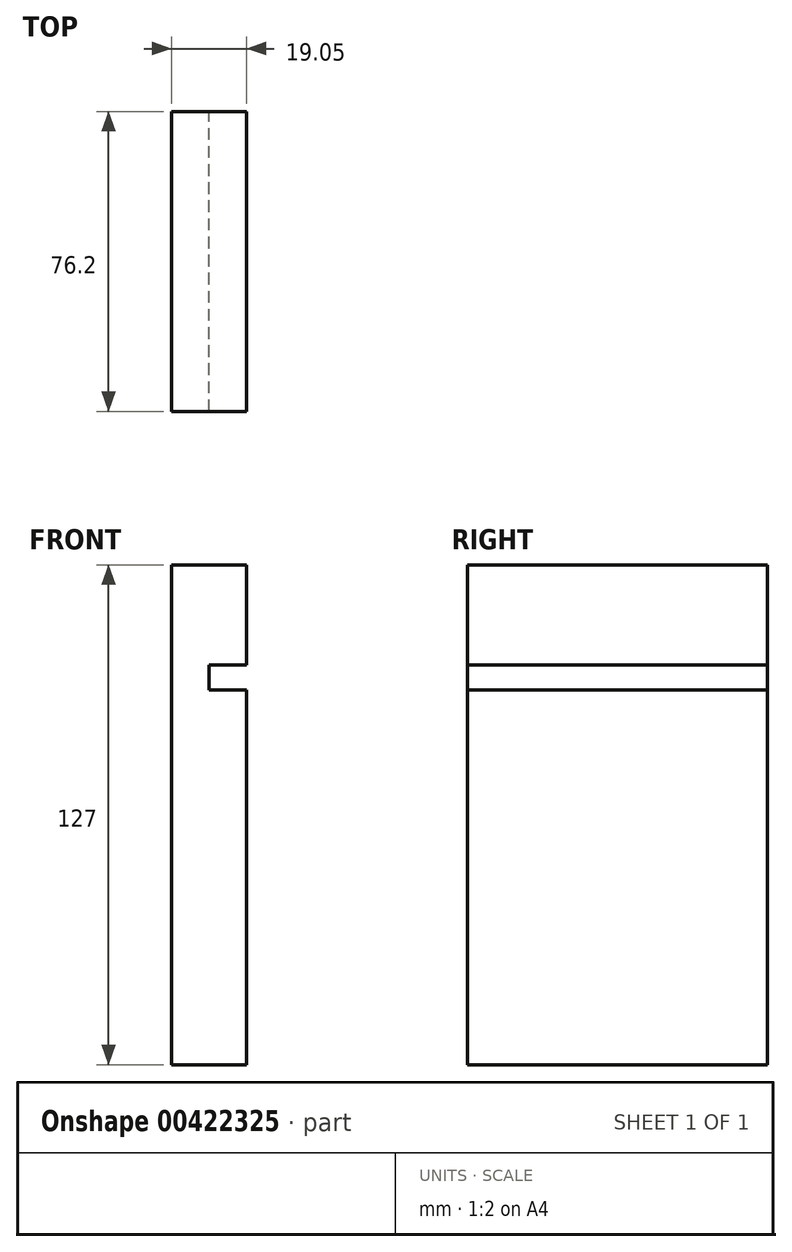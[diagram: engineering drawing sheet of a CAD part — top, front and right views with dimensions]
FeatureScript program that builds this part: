
annotation { "Feature Type Name" : "Feature", "Feature Type Description" : "" }
export const myFeature = defineFeature(function(context is Context, id is Id, definition is map)
    precondition{}
    {
        {
            var Q0;
            Q0=qCreatedBy(makeId("Front.planeOp"),FACE);
            var sketch = newSketch(context, id + "F0", { "sketchPlane" : qUnion([Q0])});
            skLineSegment(sketch, "E0", {"start": v(-41.47, 68.64) * mm, "end": v(-41.47, -58.36) * mm});
            skLineSegment(sketch, "E1", {"start": v(-41.47, 68.64) * mm, "end": v(-22.42, 68.64) * mm});
            skLineSegment(sketch, "E2", {"start": v(-22.42, 68.64) * mm, "end": v(-22.42, 43.24) * mm});
            skLineSegment(sketch, "E3", {"start": v(-22.42, 43.24) * mm, "end": v(-31.95, 43.24) * mm});
            skLineSegment(sketch, "E4", {"start": v(-31.95, 43.24) * mm, "end": v(-31.95, 36.89) * mm});
            skLineSegment(sketch, "E5", {"start": v(-31.95, 36.89) * mm, "end": v(-22.42, 36.89) * mm});
            skLineSegment(sketch, "E6", {"start": v(-41.47, -58.36) * mm, "end": v(-22.42, -58.36) * mm});
            skLineSegment(sketch, "E7", {"start": v(-22.42, 36.89) * mm, "end": v(-22.42, -58.36) * mm});
            skSolve(sketch);
        }
        {
            var Q0;
            Q0=makeQuery(id+"F0.imprint","IMPRINT",FACE,{"disambiguationData":[TD([[makeQuery(id+"F0.imprint","IMPRINT",EDGE,{"derivedFrom":sQuery(id+"F0.wireOp",EDGE,"E0")}),1.0]])]});
            extrude(context, id + "F1", {"entities" : qUnion([Q0]), "depth" : 76.2 * mm});
        }
    });
